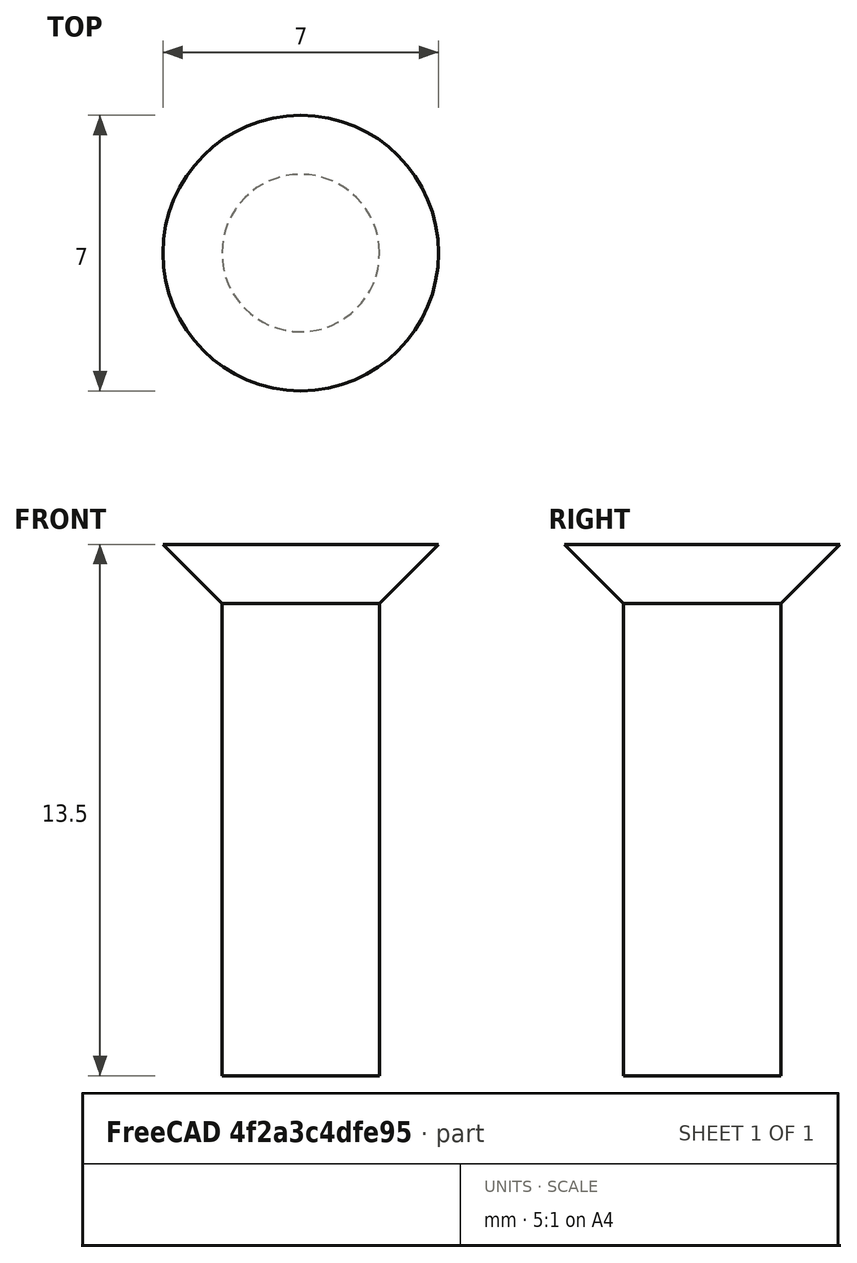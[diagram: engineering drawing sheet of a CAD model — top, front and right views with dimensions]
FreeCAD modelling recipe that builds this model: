
FCSTD DOCUMENT  (FreeCAD 0.18R14555 (Git shallow))
Label: m4-12
License: All rights reserved
LicenseURL: http://en.wikipedia.org/wiki/All_rights_reserved
objects: Sketcher::SketchObject×1, PartDesign::Revolution×1, PartDesign::Body×1
note: 4 computed .brp shape members not serialized (recipe doc carries the construction recipe); baked Part::Feature solids carry a one-line shape summary decoded from their .brp

FEATURE [Sketcher::SketchObject] Sketch
  MapMode = 5
  Placement = pos=(0,0,0) rot=(1,0,0;1.5708rad)
  Support = -> [XZ_Plane]
  sketch-geometry (5):
    g0: LineSegment StartX=0 StartY=0 StartZ=0 EndX=2 EndY=0 EndZ=0
    g1: LineSegment StartX=2 StartY=0 StartZ=0 EndX=2 EndY=12 EndZ=0
    g2: LineSegment StartX=2 StartY=12 StartZ=0 EndX=3.5 EndY=13.5 EndZ=0
    g3: LineSegment StartX=3.5 StartY=13.5 StartZ=0 EndX=0 EndY=13.5 EndZ=0
    g4: LineSegment StartX=0 StartY=13.5 StartZ=0 EndX=0 EndY=0 EndZ=0
  constraints (14):
    c: Horizontal(g0)
    c: Coincident(g0,g1)
    c: Vertical(g1)
    c: Coincident(g1,g2)
    c: Coincident(g2,g3)
    c: Horizontal(g3)
    c: Coincident(g3,g4)
    c: Coincident(g4,g0)
    c: Vertical(g4)
    c: DistanceX(g0,g0) = 2
    c: Coincident(g0,g-1)
    c: DistanceY(g1,g1) = 12
    c: DistanceX(g3,g3) = 3.5
    c: Angle(g1,g2) = 2.35619
FEATURE [PartDesign::Revolution] Revolution
  Angle = 360
  Axis = (0,2e-16,1)
  Base = (0,0,0)
  Placement = pos=(0,0,0) rot=(1,0,0;1.5708rad)
  Profile = -> Sketch
  ReferenceAxis = -> Sketch [V_Axis]
  Reversed = true
FEATURE [PartDesign::Body] Body
  Group = -> [Sketch,Revolution]
  Origin = -> Origin
  Tip = -> Revolution
